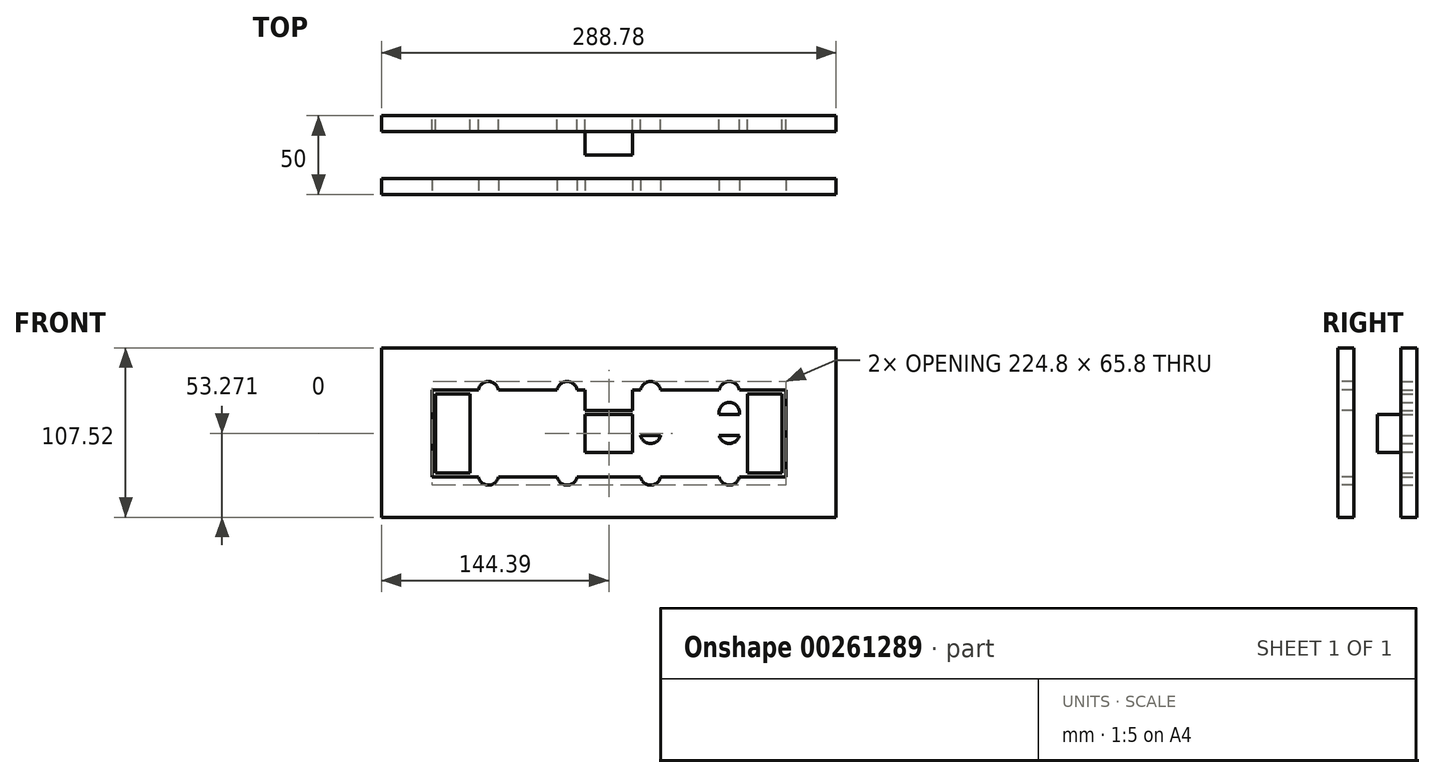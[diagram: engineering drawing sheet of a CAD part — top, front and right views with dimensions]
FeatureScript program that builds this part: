
annotation { "Feature Type Name" : "Feature", "Feature Type Description" : "" }
export const myFeature = defineFeature(function(context is Context, id is Id, definition is map)
    precondition{}
    {
        {
            var Q0;
            Q0=qCreatedBy(makeId("Front.planeOp"),FACE);
            var sketch = newSketch(context, id + "F0", { "sketchPlane" : qUnion([Q0])});
            skLineSegment(sketch, "E0.bottom", {"start": v(112.4, 0) * mm, "end": v(-112.4, 0) * mm});
            skLineSegment(sketch, "E0.top", {"start": v(112.4, 25.62) * mm, "end": v(-112.4, 25.62) * mm});
            skLineSegment(sketch, "E0.left", {"start": v(112.4, 0) * mm, "end": v(112.4, 25.62) * mm});
            skLineSegment(sketch, "E0.right", {"start": v(-112.4, 0) * mm, "end": v(-112.4, 25.62) * mm});
            skPoint(sketch, "E0.middle", {"position": v(0, 12.81) * mm});
            skLineSegment(sketch, "E1.bottom", {"start": v(15, 25.62) * mm, "end": v(-15, 25.62) * mm});
            skLineSegment(sketch, "E1.top", {"start": v(15, 38.82) * mm, "end": v(-15, 38.82) * mm});
            skLineSegment(sketch, "E1.left", {"start": v(15, 25.62) * mm, "end": v(15, 38.82) * mm});
            skLineSegment(sketch, "E1.right", {"start": v(-15, 25.62) * mm, "end": v(-15, 38.82) * mm});
            skPoint(sketch, "E1.middle", {"position": v(0, 32.22) * mm});
            skLineSegment(sketch, "E2.bottom", {"start": v(-15, 28.12) * mm, "end": v(-88.1, 28.12) * mm});
            skLineSegment(sketch, "E2.top", {"start": v(-15, 38.82) * mm, "end": v(-88.1, 38.82) * mm});
            skLineSegment(sketch, "E2.left", {"start": v(-15, 28.12) * mm, "end": v(-15, 38.82) * mm});
            skLineSegment(sketch, "E2.right", {"start": v(-88.1, 28.12) * mm, "end": v(-88.1, 38.82) * mm});
            skLineSegment(sketch, "E3.bottom", {"start": v(-88.1, 28.12) * mm, "end": v(-109.9, 28.12) * mm});
            skLineSegment(sketch, "E3.top", {"start": v(-88.1, 78.42) * mm, "end": v(-109.9, 78.42) * mm});
            skLineSegment(sketch, "E3.left", {"start": v(-88.1, 28.12) * mm, "end": v(-88.1, 78.42) * mm});
            skLineSegment(sketch, "E3.right", {"start": v(-109.9, 28.12) * mm, "end": v(-109.9, 78.42) * mm});
            skLineSegment(sketch, "E4.bottom", {"start": v(-88.1, 41.32) * mm, "end": v(-15, 41.32) * mm});
            skLineSegment(sketch, "E4.top", {"start": v(-88.1, 52.02) * mm, "end": v(-15, 52.02) * mm});
            skLineSegment(sketch, "E4.left", {"start": v(-88.1, 41.32) * mm, "end": v(-88.1, 52.02) * mm});
            skLineSegment(sketch, "E4.right", {"start": v(-15, 41.32) * mm, "end": v(-15, 52.02) * mm});
            skLineSegment(sketch, "E5.bottom", {"start": v(-15, 41.32) * mm, "end": v(15, 41.32) * mm});
            skLineSegment(sketch, "E5.top", {"start": v(-15, 65.22) * mm, "end": v(15, 65.22) * mm});
            skLineSegment(sketch, "E5.left", {"start": v(-15, 41.32) * mm, "end": v(-15, 65.22) * mm});
            skLineSegment(sketch, "E5.right", {"start": v(15, 41.32) * mm, "end": v(15, 65.22) * mm});
            skLineSegment(sketch, "E6.bottom", {"start": v(-15, 65.22) * mm, "end": v(-88.1, 65.22) * mm});
            skLineSegment(sketch, "E6.top", {"start": v(-15, 54.52) * mm, "end": v(-88.1, 54.52) * mm});
            skLineSegment(sketch, "E6.left", {"start": v(-15, 65.22) * mm, "end": v(-15, 54.52) * mm});
            skLineSegment(sketch, "E6.right", {"start": v(-88.1, 65.22) * mm, "end": v(-88.1, 54.52) * mm});
            skLineSegment(sketch, "E7.bottom", {"start": v(-88.1, 78.42) * mm, "end": v(-15, 78.42) * mm});
            skLineSegment(sketch, "E7.top", {"start": v(-88.1, 67.72) * mm, "end": v(-15, 67.72) * mm});
            skLineSegment(sketch, "E7.left", {"start": v(-88.1, 78.42) * mm, "end": v(-88.1, 67.72) * mm});
            skLineSegment(sketch, "E7.right", {"start": v(-15, 78.42) * mm, "end": v(-15, 67.72) * mm});
            skLineSegment(sketch, "E8.bottom", {"start": v(-15, 67.72) * mm, "end": v(15, 67.72) * mm});
            skLineSegment(sketch, "E8.top", {"start": v(-15, 80.92) * mm, "end": v(15, 80.92) * mm});
            skLineSegment(sketch, "E8.left", {"start": v(-15, 67.72) * mm, "end": v(-15, 80.92) * mm});
            skLineSegment(sketch, "E8.right", {"start": v(15, 67.72) * mm, "end": v(15, 80.92) * mm});
            skLineSegment(sketch, "E9", {"start": v(-15, 28.12) * mm, "end": v(-15, 25.62) * mm});
            skLineSegment(sketch, "E10", {"start": v(-15, 26.87) * mm, "end": v(-83.74, 26.87) * mm, "construction": true});
            skCircle(sketch, "E11", {"center": v(-26.5, 26.87) * mm, "radius": 6.5 * mm});
            skCircle(sketch, "E12", {"center": v(-76.5, 26.87) * mm, "radius": 6.5 * mm});
            skLineSegment(sketch, "E13", {"start": v(-88.1, 41.32) * mm, "end": v(-88.1, 38.82) * mm});
            skLineSegment(sketch, "E14", {"start": v(-88.1, 40.07) * mm, "end": v(-8.47, 40.07) * mm, "construction": true});
            skCircle(sketch, "E15", {"center": v(-26.5, 40.07) * mm, "radius": 6.5 * mm});
            skCircle(sketch, "E16", {"center": v(-76.5, 40.07) * mm, "radius": 6.5 * mm});
            skLineSegment(sketch, "E17", {"start": v(-88.1, 54.52) * mm, "end": v(-88.1, 52.02) * mm});
            skLineSegment(sketch, "E18", {"start": v(-88.1, 53.27) * mm, "end": v(-15, 53.27) * mm, "construction": true});
            skCircle(sketch, "E19", {"center": v(-76.5, 53.27) * mm, "radius": 6.5 * mm});
            skCircle(sketch, "E20", {"center": v(-26.5, 53.27) * mm, "radius": 6.5 * mm});
            skLineSegment(sketch, "E21", {"start": v(-88.1, 67.72) * mm, "end": v(-88.1, 65.22) * mm});
            skLineSegment(sketch, "E22", {"start": v(-88.1, 66.47) * mm, "end": v(-15, 66.47) * mm, "construction": true});
            skCircle(sketch, "E23", {"center": v(-76.5, 66.47) * mm, "radius": 6.5 * mm});
            skCircle(sketch, "E24", {"center": v(-26.5, 66.47) * mm, "radius": 6.5 * mm});
            skLineSegment(sketch, "E25.bottom", {"start": v(-112.4, 80.92) * mm, "end": v(112.4, 80.92) * mm});
            skLineSegment(sketch, "E25.top", {"start": v(-112.4, 107.52) * mm, "end": v(112.4, 107.52) * mm});
            skLineSegment(sketch, "E25.left", {"start": v(-112.4, 80.92) * mm, "end": v(-112.4, 107.52) * mm});
            skLineSegment(sketch, "E25.right", {"start": v(112.4, 80.92) * mm, "end": v(112.4, 107.52) * mm});
            skLineSegment(sketch, "E26", {"start": v(-15, 78.42) * mm, "end": v(-15, 80.92) * mm});
            skLineSegment(sketch, "E27", {"start": v(-15, 79.67) * mm, "end": v(-88.1, 79.67) * mm, "construction": true});
            skCircle(sketch, "E28", {"center": v(-76.5, 79.67) * mm, "radius": 6.5 * mm});
            skCircle(sketch, "E29", {"center": v(-26.5, 79.67) * mm, "radius": 6.5 * mm});
            skLineSegment(sketch, "E30.MirrorCS", {"start": v(15, 28.12) * mm, "end": v(15, 25.62) * mm});
            skLineSegment(sketch, "E31.MirrorCS", {"start": v(88.1, 41.32) * mm, "end": v(88.1, 38.82) * mm});
            skLineSegment(sketch, "E32.MirrorCS", {"start": v(15, 78.42) * mm, "end": v(15, 80.92) * mm});
            skLineSegment(sketch, "E33.MirrorCS", {"start": v(88.1, 67.72) * mm, "end": v(88.1, 65.22) * mm});
            skLineSegment(sketch, "E34.MirrorCS", {"start": v(88.1, 54.52) * mm, "end": v(88.1, 52.02) * mm});
            skLineSegment(sketch, "E35.MirrorCS", {"start": v(15, 41.32) * mm, "end": v(15, 52.02) * mm});
            skLineSegment(sketch, "E36.MirrorCS", {"start": v(88.1, 78.42) * mm, "end": v(88.1, 67.72) * mm});
            skLineSegment(sketch, "E37.MirrorCS", {"start": v(88.1, 65.22) * mm, "end": v(88.1, 54.52) * mm});
            skLineSegment(sketch, "E38.MirrorCS", {"start": v(15, 65.22) * mm, "end": v(15, 54.52) * mm});
            skLineSegment(sketch, "E39.MirrorCS", {"start": v(15, 78.42) * mm, "end": v(15, 67.72) * mm});
            skCircle(sketch, "E40.MirrorC", {"center": v(76.5, 66.47) * mm, "radius": 6.5 * mm});
            skCircle(sketch, "E41.MirrorC", {"center": v(76.5, 79.67) * mm, "radius": 6.5 * mm});
            skLineSegment(sketch, "E42.MirrorCS", {"start": v(15, 54.52) * mm, "end": v(88.1, 54.52) * mm});
            skLineSegment(sketch, "E43.MirrorCS", {"start": v(88.1, 66.47) * mm, "end": v(15, 66.47) * mm, "construction": true});
            skLineSegment(sketch, "E44.MirrorCS", {"start": v(88.1, 41.32) * mm, "end": v(88.1, 52.02) * mm});
            skLineSegment(sketch, "E45.MirrorCS", {"start": v(88.1, 52.02) * mm, "end": v(15, 52.02) * mm});
            skLineSegment(sketch, "E46.MirrorCS", {"start": v(15, 65.22) * mm, "end": v(88.1, 65.22) * mm});
            skCircle(sketch, "E47.MirrorC", {"center": v(26.5, 66.47) * mm, "radius": 6.5 * mm});
            skCircle(sketch, "E48.MirrorC", {"center": v(26.5, 40.07) * mm, "radius": 6.5 * mm});
            skLineSegment(sketch, "E49.MirrorCS", {"start": v(15, 26.87) * mm, "end": v(83.74, 26.87) * mm, "construction": true});
            skCircle(sketch, "E50.MirrorC", {"center": v(76.5, 40.07) * mm, "radius": 6.5 * mm});
            skLineSegment(sketch, "E51.MirrorCS", {"start": v(88.1, 41.32) * mm, "end": v(15, 41.32) * mm});
            skCircle(sketch, "E52.MirrorC", {"center": v(26.5, 53.27) * mm, "radius": 6.5 * mm});
            skCircle(sketch, "E53.MirrorC", {"center": v(26.5, 26.87) * mm, "radius": 6.5 * mm});
            skLineSegment(sketch, "E54.MirrorCS", {"start": v(88.1, 28.12) * mm, "end": v(88.1, 78.42) * mm});
            skCircle(sketch, "E55.MirrorC", {"center": v(76.5, 26.87) * mm, "radius": 6.5 * mm});
            skLineSegment(sketch, "E56.MirrorCS", {"start": v(15, 79.67) * mm, "end": v(88.1, 79.67) * mm, "construction": true});
            skLineSegment(sketch, "E57.MirrorCS", {"start": v(88.1, 53.27) * mm, "end": v(15, 53.27) * mm, "construction": true});
            skLineSegment(sketch, "E58.MirrorCS", {"start": v(88.1, 78.42) * mm, "end": v(109.9, 78.42) * mm});
            skCircle(sketch, "E59.MirrorC", {"center": v(26.5, 79.67) * mm, "radius": 6.5 * mm});
            skLineSegment(sketch, "E60.MirrorCS", {"start": v(88.1, 67.72) * mm, "end": v(15, 67.72) * mm});
            skCircle(sketch, "E61.MirrorC", {"center": v(76.5, 53.27) * mm, "radius": 6.5 * mm});
            skLineSegment(sketch, "E62.MirrorCS", {"start": v(88.1, 28.12) * mm, "end": v(88.1, 38.82) * mm});
            skLineSegment(sketch, "E63.MirrorCS", {"start": v(15, 28.12) * mm, "end": v(15, 38.82) * mm});
            skLineSegment(sketch, "E64.MirrorCS", {"start": v(88.1, 28.12) * mm, "end": v(109.9, 28.12) * mm});
            skLineSegment(sketch, "E65.MirrorCS", {"start": v(88.1, 78.42) * mm, "end": v(15, 78.42) * mm});
            skLineSegment(sketch, "E66.MirrorCS", {"start": v(15, 38.82) * mm, "end": v(88.1, 38.82) * mm});
            skLineSegment(sketch, "E67.MirrorCS", {"start": v(15, 28.12) * mm, "end": v(88.1, 28.12) * mm});
            skLineSegment(sketch, "E68.MirrorCS", {"start": v(109.9, 28.12) * mm, "end": v(109.9, 78.42) * mm});
            skLineSegment(sketch, "E69.bottom", {"start": v(-112.4, 107.52) * mm, "end": v(-144.4, 107.52) * mm});
            skLineSegment(sketch, "E69.top", {"start": v(-112.4, 0) * mm, "end": v(-144.4, 0) * mm});
            skLineSegment(sketch, "E69.left", {"start": v(-112.4, 107.52) * mm, "end": v(-112.4, 0) * mm});
            skLineSegment(sketch, "E69.right", {"start": v(-144.4, 107.52) * mm, "end": v(-144.4, 0) * mm});
            skLineSegment(sketch, "E70.MirrorCS", {"start": v(144.4, 107.52) * mm, "end": v(144.4, 0) * mm});
            skLineSegment(sketch, "E71.MirrorCS", {"start": v(112.4, 0) * mm, "end": v(144.4, 0) * mm});
            skLineSegment(sketch, "E72", {"start": v(112.4, 107.52) * mm, "end": v(144.4, 107.52) * mm});
            skLineSegment(sketch, "E73", {"start": v(112.4, 80.92) * mm, "end": v(112.4, 25.62) * mm});
            skSolve(sketch);
        }
        {
            var Q0;
            {var subQ3=sQuery(id+"F0.wireOp",EDGE,"E69.bottom");Q0=makeQuery(id+"F0.imprint","IMPRINT",FACE,{"disambiguationData":[TD([[makeQuery(id+"F0.imprint","IMPRINT",EDGE,{"derivedFrom":subQ3}),1.0]])]});}
            var Q1;
            {var subQ14=sQuery(id+"F0.wireOp",EDGE,"E25.top");Q1=makeQuery(id+"F0.imprint","IMPRINT",FACE,{"disambiguationData":[TD([[makeQuery(id+"F0.imprint","IMPRINT",EDGE,{"derivedFrom":subQ14}),-1.0]])]});}
            var Q2;
            Q2=makeQuery(id+"F0.imprint","IMPRINT",FACE,{"disambiguationData":[TD([[makeQuery(id+"F0.imprint","IMPRINT",EDGE,{"derivedFrom":sQuery(id+"F0.wireOp",EDGE,"E0.left")}),-1.0]])]});
            var Q3;
            {var subQ6=sQuery(id+"F0.wireOp",EDGE,"E0.bottom");Q3=makeQuery(id+"F0.imprint","IMPRINT",FACE,{"disambiguationData":[TD([[makeQuery(id+"F0.imprint","IMPRINT",EDGE,{"derivedFrom":subQ6}),-1.0]])]});}
            var Q4;
            Q4=makeQuery(id+"F0.imprint","IMPRINT",FACE,{"disambiguationData":[TD([[makeQuery(id+"F0.imprint","IMPRINT",EDGE,{"derivedFrom":sQuery(id+"F0.wireOp",EDGE,"E1.bottom")}),-1.0]])]});
            var Q5;
            {var subQ7=sQuery(id+"F0.wireOp",EDGE,"E58.MirrorCS");Q5=makeQuery(id+"F0.imprint","IMPRINT",FACE,{"disambiguationData":[TD([[makeQuery(id+"F0.imprint","IMPRINT",EDGE,{"derivedFrom":subQ7}),-1.0]])]});}
            var Q6;
            {var subQ5=sQuery(id+"F0.wireOp",EDGE,"E60.MirrorCS");var subQ11=sQuery(id+"F0.wireOp",EDGE,"E40.MirrorC");var subQ12=makeQuery(id+"F0.imprint","INTERSECT",VERTEX,{"disambiguationData":[OD(0.0)],"derivedFrom":[subQ11,subQ5]});Q6=makeQuery(id+"F0.imprint","IMPRINT",FACE,{"disambiguationData":[TD([[makeQuery(id+"F0.imprint","IMPRINT",EDGE,{"disambiguationData":[TD([[subQ12,1.0]])],"derivedFrom":subQ11}),1.0]])]});}
            var Q7;
            {var subQ5=sQuery(id+"F0.wireOp",EDGE,"E46.MirrorCS");var subQ10=sQuery(id+"F0.wireOp",EDGE,"E40.MirrorC");var subQ14=makeQuery(id+"F0.imprint","INTERSECT",VERTEX,{"disambiguationData":[OD(0.0)],"derivedFrom":[subQ10,subQ5]});Q7=makeQuery(id+"F0.imprint","IMPRINT",FACE,{"disambiguationData":[TD([[makeQuery(id+"F0.imprint","IMPRINT",EDGE,{"disambiguationData":[TD([[subQ14,-1.0]])],"derivedFrom":subQ10}),1.0]])]});}
            var Q8;
            {var subQ1=sQuery(id+"F0.wireOp",EDGE,"E45.MirrorCS");var subQ4=sQuery(id+"F0.wireOp",EDGE,"E54.MirrorCS");var subQ16=makeQuery(id+"F0.imprint","INTERSECT",VERTEX,{"derivedFrom":[subQ1,subQ4]});Q8=makeQuery(id+"F0.imprint","IMPRINT",FACE,{"disambiguationData":[TD([[makeQuery(id+"F0.imprint","IMPRINT",EDGE,{"disambiguationData":[TD([[subQ16,-1.0]])],"derivedFrom":subQ1}),1.0]])]});}
            var Q9;
            {var subQ1=sQuery(id+"F0.wireOp",EDGE,"E62.MirrorCS");Q9=makeQuery(id+"F0.imprint","IMPRINT",FACE,{"disambiguationData":[TD([[makeQuery(id+"F0.imprint","IMPRINT",EDGE,{"derivedFrom":subQ1}),1.0]])]});}
            var Q10;
            {var subQ4=sQuery(id+"F0.wireOp",EDGE,"E2.left");Q10=makeQuery(id+"F0.imprint","IMPRINT",FACE,{"disambiguationData":[TD([[makeQuery(id+"F0.imprint","IMPRINT",EDGE,{"derivedFrom":subQ4}),1.0]])]});}
            var Q11;
            {var subQ14=sQuery(id+"F0.wireOp",EDGE,"E4.left");Q11=makeQuery(id+"F0.imprint","IMPRINT",FACE,{"disambiguationData":[TD([[makeQuery(id+"F0.imprint","IMPRINT",EDGE,{"derivedFrom":subQ14}),-1.0]])]});}
            var Q12;
            {var subQ6=sQuery(id+"F0.wireOp",EDGE,"E6.left");Q12=makeQuery(id+"F0.imprint","IMPRINT",FACE,{"disambiguationData":[TD([[makeQuery(id+"F0.imprint","IMPRINT",EDGE,{"derivedFrom":subQ6}),-1.0]])]});}
            var Q13;
            {var subQ4=sQuery(id+"F0.wireOp",EDGE,"E7.left");Q13=makeQuery(id+"F0.imprint","IMPRINT",FACE,{"disambiguationData":[TD([[makeQuery(id+"F0.imprint","IMPRINT",EDGE,{"derivedFrom":subQ4}),1.0]])]});}
            var Q14;
            Q14=makeQuery(id+"F0.imprint","IMPRINT",FACE,{"disambiguationData":[TD([[makeQuery(id+"F0.imprint","IMPRINT",EDGE,{"derivedFrom":sQuery(id+"F0.wireOp",EDGE,"E3.bottom")}),-1.0]])]});
            var Q15;
            {var subQ4=sQuery(id+"F0.wireOp",EDGE,"E8.bottom");Q15=makeQuery(id+"F0.imprint","IMPRINT",FACE,{"disambiguationData":[TD([[makeQuery(id+"F0.imprint","IMPRINT",EDGE,{"derivedFrom":subQ4}),1.0]])]});}
            extrude(context, id + "F1", {"entities" : qUnion([Q0, Q1, Q2, Q3, Q4, Q5, Q6, Q7, Q8, Q9, Q10, Q11, Q12, Q13, Q14, Q15]), "depth" : 10 * mm});
        }
        {
            var Q0;
            {var subQ3=sQuery(id+"F0.wireOp",EDGE,"E5.bottom");Q0=makeQuery(id+"F0.imprint","IMPRINT",FACE,{"disambiguationData":[TD([[makeQuery(id+"F0.imprint","IMPRINT",EDGE,{"derivedFrom":subQ3}),1.0]])]});}
            extrude(context, id + "F2", {"entities" : qUnion([Q0]), "operationType" : NewBodyOperationType.ADD, "depth" : 25 * mm});
        }
        {
            var Q0;
            Q0=makeQuery(id+"F1.opExtrude","SWEPT_BODY",BODY,{"disambiguationData":[OSD([sQuery(id+"F0.wireOp",EDGE,"E0.bottom"),sQuery(id+"F0.wireOp",EDGE,"E0.top"),sQuery(id+"F0.wireOp",EDGE,"E1.top"),sQuery(id+"F0.wireOp",EDGE,"E2.bottom"),sQuery(id+"F0.wireOp",EDGE,"E2.top"),sQuery(id+"F0.wireOp",EDGE,"E3.bottom"),sQuery(id+"F0.wireOp",EDGE,"E3.top"),sQuery(id+"F0.wireOp",EDGE,"E3.right"),sQuery(id+"F0.wireOp",EDGE,"E4.bottom"),sQuery(id+"F0.wireOp",EDGE,"E4.top"),sQuery(id+"F0.wireOp",EDGE,"E5.left"),sQuery(id+"F0.wireOp",EDGE,"E6.bottom"),sQuery(id+"F0.wireOp",EDGE,"E6.top"),sQuery(id+"F0.wireOp",EDGE,"E6.left"),sQuery(id+"F0.wireOp",EDGE,"E7.bottom"),sQuery(id+"F0.wireOp",EDGE,"E7.top"),sQuery(id+"F0.wireOp",EDGE,"E8.bottom"),sQuery(id+"F0.wireOp",EDGE,"E9"),sQuery(id+"F0.wireOp",EDGE,"E11"),sQuery(id+"F0.wireOp",EDGE,"E12"),sQuery(id+"F0.wireOp",EDGE,"E13"),sQuery(id+"F0.wireOp",EDGE,"E15"),sQuery(id+"F0.wireOp",EDGE,"E16"),sQuery(id+"F0.wireOp",EDGE,"E17"),sQuery(id+"F0.wireOp",EDGE,"E19"),sQuery(id+"F0.wireOp",EDGE,"E20"),sQuery(id+"F0.wireOp",EDGE,"E21"),sQuery(id+"F0.wireOp",EDGE,"E23"),sQuery(id+"F0.wireOp",EDGE,"E24"),sQuery(id+"F0.wireOp",EDGE,"E25.bottom"),sQuery(id+"F0.wireOp",EDGE,"E25.top"),sQuery(id+"F0.wireOp",EDGE,"E26"),sQuery(id+"F0.wireOp",EDGE,"E28"),sQuery(id+"F0.wireOp",EDGE,"E29"),sQuery(id+"F0.wireOp",EDGE,"E1.left"),sQuery(id+"F0.wireOp",EDGE,"E8.right"),sQuery(id+"F0.wireOp",EDGE,"E40.MirrorC"),sQuery(id+"F0.wireOp",EDGE,"E41.MirrorC"),sQuery(id+"F0.wireOp",EDGE,"E42.MirrorCS"),sQuery(id+"F0.wireOp",EDGE,"E45.MirrorCS"),sQuery(id+"F0.wireOp",EDGE,"E46.MirrorCS"),sQuery(id+"F0.wireOp",EDGE,"E47.MirrorC"),sQuery(id+"F0.wireOp",EDGE,"E48.MirrorC"),sQuery(id+"F0.wireOp",EDGE,"E50.MirrorC"),sQuery(id+"F0.wireOp",EDGE,"E51.MirrorCS"),sQuery(id+"F0.wireOp",EDGE,"E52.MirrorC"),sQuery(id+"F0.wireOp",EDGE,"E53.MirrorC"),sQuery(id+"F0.wireOp",EDGE,"E5.right"),sQuery(id+"F0.wireOp",EDGE,"E54.MirrorCS"),sQuery(id+"F0.wireOp",EDGE,"E55.MirrorC"),sQuery(id+"F0.wireOp",EDGE,"E58.MirrorCS"),sQuery(id+"F0.wireOp",EDGE,"E59.MirrorC"),sQuery(id+"F0.wireOp",EDGE,"E60.MirrorCS"),sQuery(id+"F0.wireOp",EDGE,"E61.MirrorC"),sQuery(id+"F0.wireOp",EDGE,"E64.MirrorCS"),sQuery(id+"F0.wireOp",EDGE,"E65.MirrorCS"),sQuery(id+"F0.wireOp",EDGE,"E66.MirrorCS"),sQuery(id+"F0.wireOp",EDGE,"E67.MirrorCS"),sQuery(id+"F0.wireOp",EDGE,"E68.MirrorCS"),sQuery(id+"F0.wireOp",EDGE,"E69.bottom"),sQuery(id+"F0.wireOp",EDGE,"E69.top"),sQuery(id+"F0.wireOp",EDGE,"E69.left"),sQuery(id+"F0.wireOp",EDGE,"E69.right"),sQuery(id+"F0.wireOp",EDGE,"E70.MirrorCS"),sQuery(id+"F0.wireOp",EDGE,"E71.MirrorCS"),sQuery(id+"F0.wireOp",EDGE,"E72"),sQuery(id+"F0.wireOp",EDGE,"E73")])]});
            var Q1;
            Q1=makeQuery(id+"F2.opExtrude","CAP_FACE",FACE,{"disambiguationData":[OSD([sQuery(id+"F0.wireOp",EDGE,"E5.bottom"),sQuery(id+"F0.wireOp",EDGE,"E5.top"),sQuery(id+"F0.wireOp",EDGE,"E5.left"),sQuery(id+"F0.wireOp",EDGE,"E6.left"),sQuery(id+"F0.wireOp",EDGE,"E5.right")])],"isStart":false});
            mirror(context, id + "F3", {"operationType" : NewBodyOperationType.ADD, "entities" : qUnion([Q0]), "mirrorPlane" : qUnion([Q1])});
        }
        {
            var Q0;
            {var subQ0=sQuery(id+"F0.wireOp",EDGE,"E5.bottom");var subQ1=sQuery(id+"F0.wireOp",EDGE,"E51.MirrorCS");var subQ2=sQuery(id+"F0.wireOp",EDGE,"E4.bottom");var subQ3=makeQuery(id+"F2.boolean.opBoolean","MERGE",FACE,{"derivedFrom":[makeQuery(id+"F1.opExtrude","SWEPT_FACE",FACE,{"disambiguationData":[OSD([subQ2]),TDD([makeQuery(id+"F0.imprint","IMPRINT",EDGE,{"disambiguationData":[TD([[makeQuery(id+"F0.imprint","INTERSECT",VERTEX,{"disambiguationData":[OD(1.0)],"derivedFrom":[subQ2,sQuery(id+"F0.wireOp",EDGE,"E15")]}),-1.0]])],"derivedFrom":subQ2})])]}),makeQuery(id+"F1.opExtrude","SWEPT_FACE",FACE,{"disambiguationData":[OSD([subQ1]),TDD([makeQuery(id+"F0.imprint","IMPRINT",EDGE,{"disambiguationData":[TD([[makeQuery(id+"F0.imprint","INTERSECT",VERTEX,{"disambiguationData":[OD(1.0)],"derivedFrom":[sQuery(id+"F0.wireOp",EDGE,"E48.MirrorC"),subQ1]}),-1.0]])],"derivedFrom":subQ1})])]}),makeQuery(id+"F2.opExtrude","SWEPT_FACE",FACE,{"disambiguationData":[OSD([subQ0])]})]});Q0=makeQuery(id+"F3.boolean.opBoolean","MERGE",FACE,{"derivedFrom":[subQ3,makeQuery(id+"F3.opPattern","COPY",FACE,{"derivedFrom":subQ3,"instanceName":"1"})]});}
            var sketch = newSketch(context, id + "F4", { "sketchPlane" : qUnion([Q0])});
            skLineSegment(sketch, "E74.bottom", {"start": v(-15, 10) * mm, "end": v(15, 10) * mm});
            skLineSegment(sketch, "E74.top", {"start": v(-15, 40) * mm, "end": v(15, 40) * mm});
            skLineSegment(sketch, "E74.left", {"start": v(-15, 10) * mm, "end": v(-15, 40) * mm});
            skLineSegment(sketch, "E74.right", {"start": v(15, 10) * mm, "end": v(15, 40) * mm});
            skSolve(sketch);
        }
        {
            var Q0;
            Q0=makeQuery(id+"F4.imprint","IMPRINT",FACE,{"disambiguationData":[TD([[makeQuery(id+"F4.imprint","IMPRINT",EDGE,{"derivedFrom":sQuery(id+"F4.wireOp",EDGE,"E74.bottom")}),1.0]])]});
            extrude(context, id + "F5", {"entities" : qUnion([Q0]), "operationType" : NewBodyOperationType.ADD, "depth" : 0.1 * mm});
        }
    });
